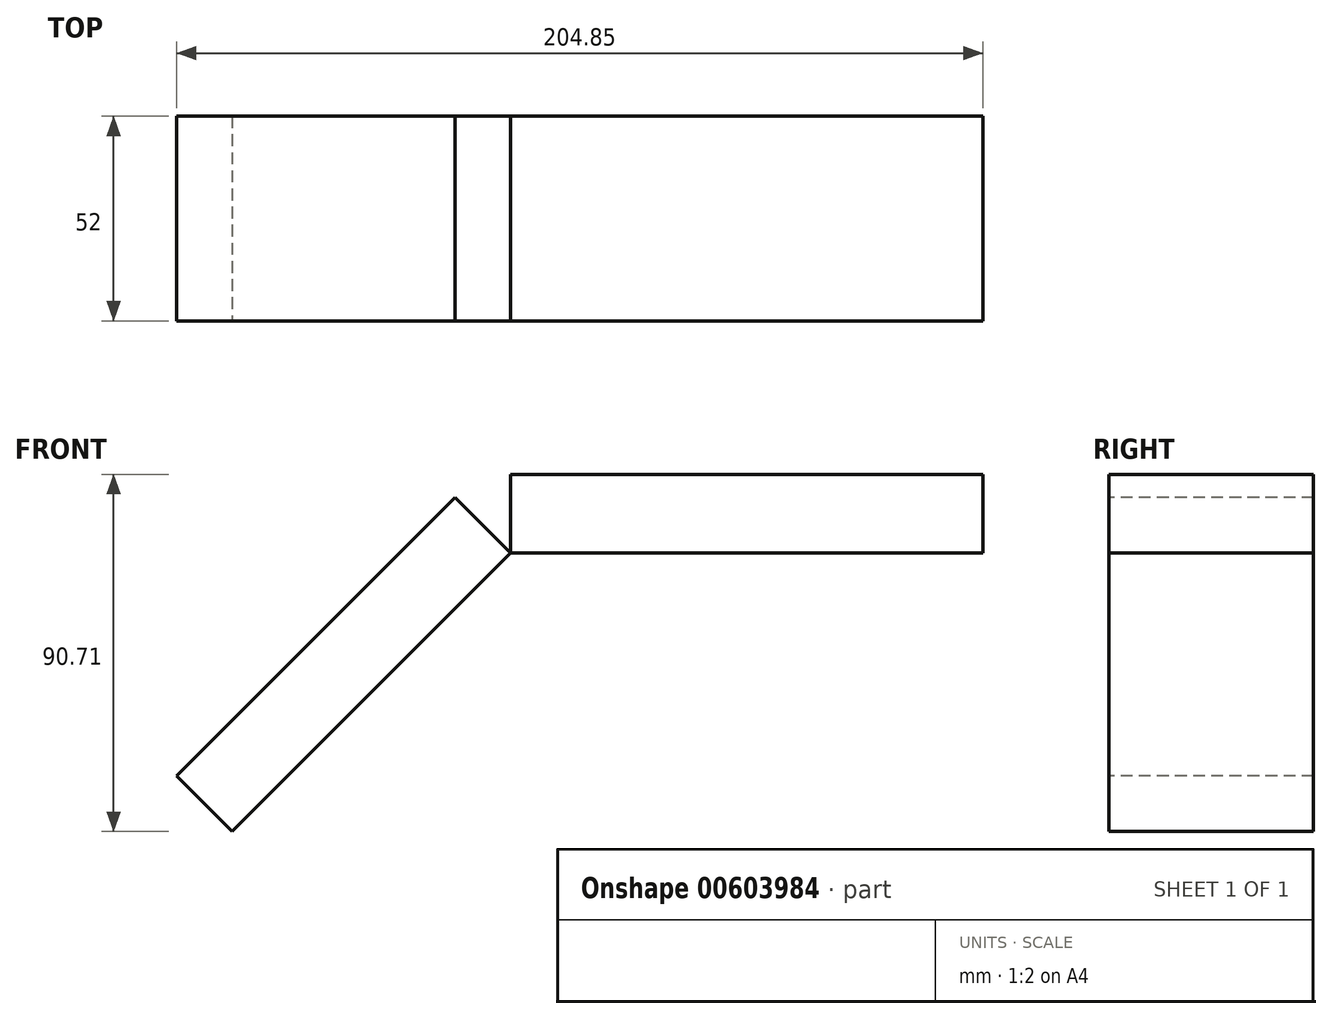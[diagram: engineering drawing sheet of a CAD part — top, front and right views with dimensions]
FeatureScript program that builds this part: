
annotation { "Feature Type Name" : "Feature", "Feature Type Description" : "" }
export const myFeature = defineFeature(function(context is Context, id is Id, definition is map)
    precondition{}
    {
        {
            var Q0;
            Q0=qCreatedBy(makeId("Front.planeOp"),FACE);
            var sketch = newSketch(context, id + "F0", { "sketchPlane" : qUnion([Q0])});
            skLineSegment(sketch, "E0.bottom", {"start": v(51.22, 11.17) * mm, "end": v(-68.78, 11.17) * mm});
            skLineSegment(sketch, "E0.top", {"start": v(51.22, -8.83) * mm, "end": v(-68.78, -8.83) * mm});
            skLineSegment(sketch, "E0.left", {"start": v(51.22, 11.17) * mm, "end": v(51.22, -8.83) * mm});
            skLineSegment(sketch, "E0.right", {"start": v(-68.78, 11.17) * mm, "end": v(-68.78, -8.83) * mm});
            skPoint(sketch, "E1", {"position": v(-68.78, 11.17) * mm});
            skSolve(sketch);
        }
        {
            var Q0;
            Q0=qCreatedBy(makeId("Front.planeOp"),FACE);
            var sketch = newSketch(context, id + "F1", { "sketchPlane" : qUnion([Q0])});
            skPoint(sketch, "E2.0", {"position": v(-68.78, 11.17) * mm});
            skPoint(sketch, "E3.0", {"position": v(-68.78, -8.83) * mm});
            skLineSegment(sketch, "E4.bottom", {"start": v(-68.78, 11.17) * mm, "end": v(-168.78, 11.17) * mm});
            skLineSegment(sketch, "E4.top", {"start": v(-68.78, -8.83) * mm, "end": v(-168.78, -8.83) * mm});
            skLineSegment(sketch, "E4.left", {"start": v(-68.78, 11.17) * mm, "end": v(-68.78, -8.83) * mm});
            skLineSegment(sketch, "E4.right", {"start": v(-168.78, 11.17) * mm, "end": v(-168.78, -8.83) * mm});
            skSolve(sketch);
        }
        {
            var Q0;
            Q0=makeQuery(id+"F1.imprint","IMPRINT",FACE,{"disambiguationData":[TD([[makeQuery(id+"F1.imprint","IMPRINT",EDGE,{"derivedFrom":sQuery(id+"F1.wireOp",EDGE,"E4.bottom")}),1.0]])]});
            var Q1;
            Q1=makeQuery(id+"F0.imprint","IMPRINT",FACE,{"disambiguationData":[TD([[makeQuery(id+"F0.imprint","IMPRINT",EDGE,{"derivedFrom":sQuery(id+"F0.wireOp",EDGE,"E0.bottom")}),1.0]])]});
            extrude(context, id + "F2", {"entities" : qUnion([Q0, Q1]), "depth" : 52 * mm, "offsetDistance" : 25 * mm});
        }
        {
            var Q0;
            Q0=makeQuery(id+"F2.opExtrude","SWEPT_BODY",BODY,{"disambiguationData":[OSD([sQuery(id+"F1.wireOp",EDGE,"E4.bottom"),sQuery(id+"F1.wireOp",EDGE,"E4.top"),sQuery(id+"F1.wireOp",EDGE,"E4.left"),sQuery(id+"F1.wireOp",EDGE,"E4.right")])]});
            var Q1;
            Q1=makeQuery(id+"F2.opExtrude","CAP_VERTEX",VERTEX,{"disambiguationData":[OSD([sQuery(id+"F0.wireOp",EDGE,"E0.bottom"),sQuery(id+"F0.wireOp",EDGE,"E0.right")])],"isStart":false});
            var Q2;
            Q2=makeQuery(id+"F2.opExtrude","SWEPT_EDGE",EDGE,{"disambiguationData":[OSD([sQuery(id+"F0.wireOp",EDGE,"E0.bottom"),sQuery(id+"F0.wireOp",EDGE,"E0.right")])]});
            transform(context, id + "F3", {"entities" : qUnion([Q0]), "transformType" : TransformType.ROTATION, "transformAxis" : qUnion([Q2]), "angle" : 45 * degree, "makeCopy" : false});
        }
        {
            var Q0;
            Q0=makeQuery(id+"F2.opExtrude","SWEPT_BODY",BODY,{"disambiguationData":[OSD([sQuery(id+"F1.wireOp",EDGE,"E4.bottom"),sQuery(id+"F1.wireOp",EDGE,"E4.top"),sQuery(id+"F1.wireOp",EDGE,"E4.left"),sQuery(id+"F1.wireOp",EDGE,"E4.right")])]});
            var Q1;
            Q1=makeQuery(id+"F2.opExtrude","SWEPT_BODY",BODY,{"disambiguationData":[OSD([sQuery(id+"F0.wireOp",EDGE,"E0.bottom"),sQuery(id+"F0.wireOp",EDGE,"E0.top"),sQuery(id+"F0.wireOp",EDGE,"E0.left"),sQuery(id+"F0.wireOp",EDGE,"E0.right")])]});
            var Q2;
            Q2=makeQuery(id+"F2.opExtrude","CAP_EDGE",EDGE,{"disambiguationData":[OSD([sQuery(id+"F0.wireOp",EDGE,"E0.bottom")])],"isStart":false});
            transform(context, id + "F4", {"entities" : qUnion([Q0, Q1]), "transformType" : TransformType.ROTATION, "transformAxis" : qUnion([Q2]), "angle" : 180 * degree, "makeCopy" : false});
        }
    });
